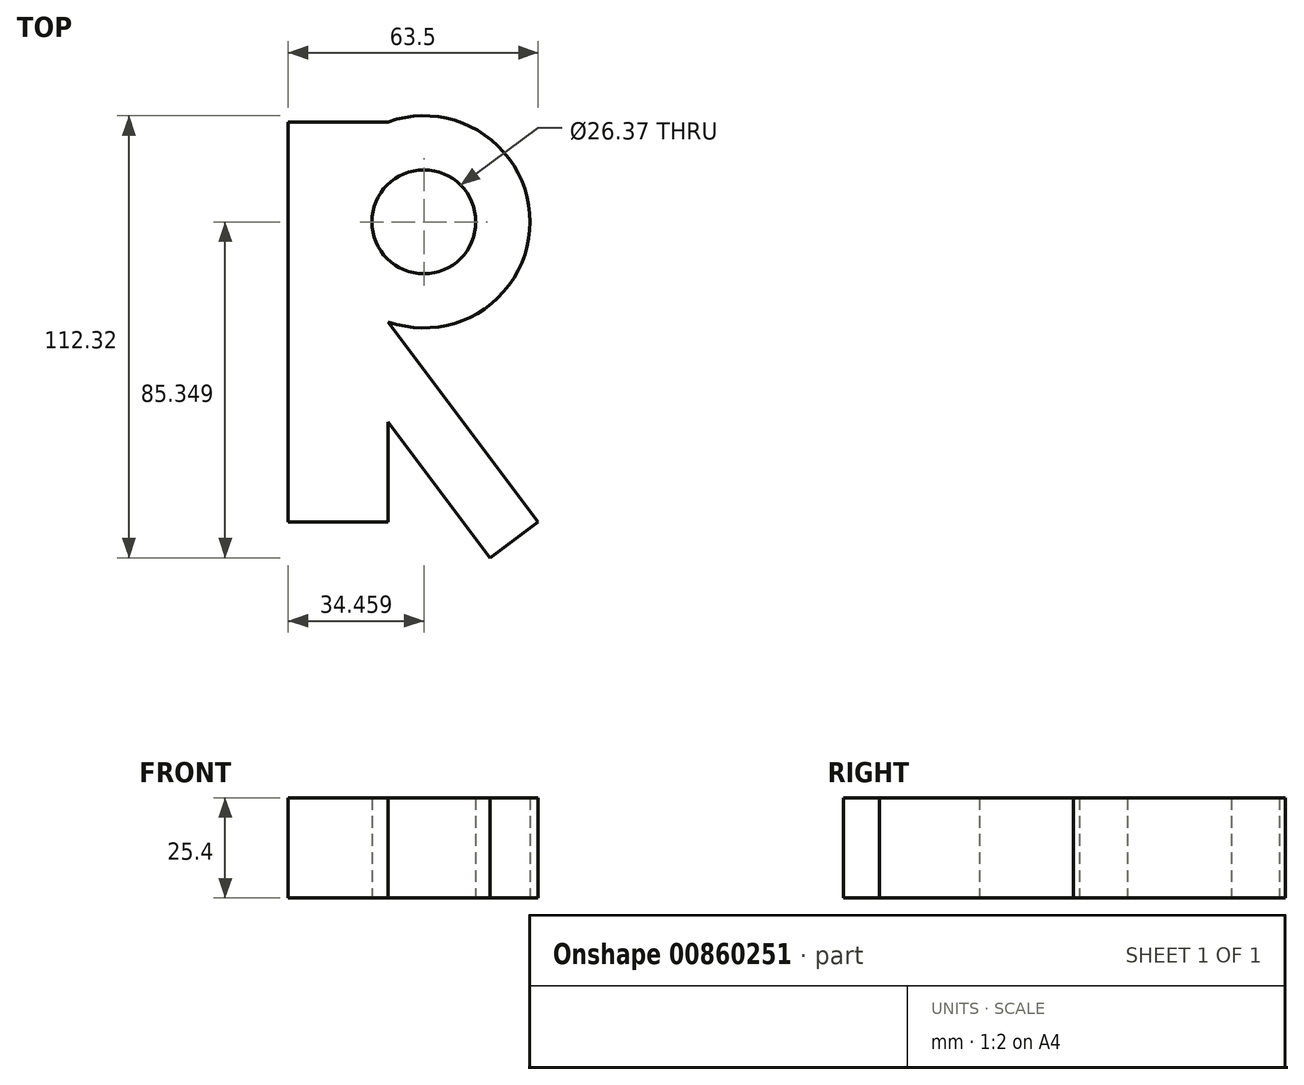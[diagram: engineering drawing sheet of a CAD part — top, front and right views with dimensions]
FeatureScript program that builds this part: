
annotation { "Feature Type Name" : "Feature", "Feature Type Description" : "" }
export const myFeature = defineFeature(function(context is Context, id is Id, definition is map)
    precondition{}
    {
        {
            var Q0;
            Q0=qCreatedBy(makeId("Top.planeOp"),FACE);
            var sketch = newSketch(context, id + "F0", { "sketchPlane" : qUnion([Q0])});
            skLineSegment(sketch, "E0", {"start": v(-43.15, -52.76) * mm, "end": v(-43.15, -1.96) * mm});
            skLineSegment(sketch, "E1", {"start": v(-43.15, -1.96) * mm, "end": v(-5.05, -52.76) * mm});
            skArc(sketch, "E2", {"start": v(-43.15, -1.96) * mm, "mid": v(-7.12, 23.44) * mm, "end": v(-43.15, 48.84) * mm});
            skLineSegment(sketch, "E3", {"start": v(-43.15, -52.76) * mm, "end": v(-68.55, -52.76) * mm});
            skLineSegment(sketch, "E4", {"start": v(-68.55, -52.76) * mm, "end": v(-68.55, 48.84) * mm});
            skLineSegment(sketch, "E5", {"start": v(-68.55, 48.84) * mm, "end": v(-43.15, 48.84) * mm});
            skLineSegment(sketch, "E6", {"start": v(-5.05, -52.76) * mm, "end": v(-17.24, -61.9) * mm});
            skLineSegment(sketch, "E7", {"start": v(-17.24, -61.9) * mm, "end": v(-43.15, -27.36) * mm});
            skCircle(sketch, "E8", {"center": v(-34.1, 23.44) * mm, "radius": 13.19 * mm});
            skSolve(sketch);
        }
        {
            var Q0;
            Q0 = qSketchRegion(id + "F0", true);
            extrude(context, id + "F1", {"entities" : qUnion([Q0]), "depth" : 25.4 * mm, "offsetDistance" : 25.4 * mm});
        }
    });
